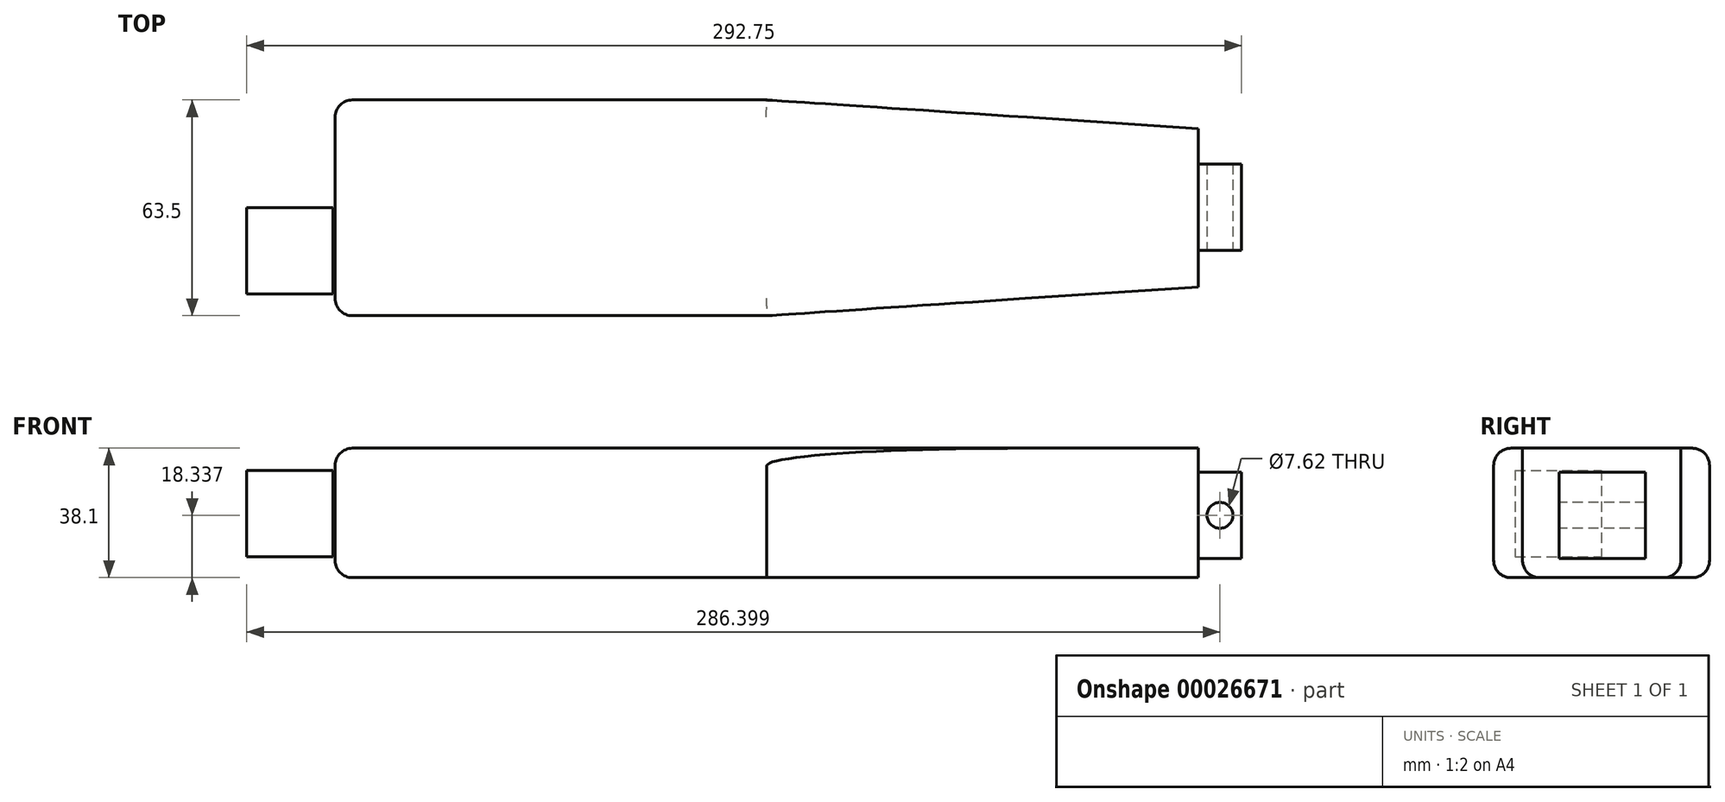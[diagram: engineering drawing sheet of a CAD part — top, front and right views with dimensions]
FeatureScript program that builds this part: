
annotation { "Feature Type Name" : "Feature", "Feature Type Description" : "" }
export const myFeature = defineFeature(function(context is Context, id is Id, definition is map)
    precondition{}
    {
        {
            var Q0;
            Q0=qCreatedBy(makeId("Front.planeOp"),FACE);
            var sketch = newSketch(context, id + "F0", { "sketchPlane" : qUnion([Q0])});
            skLineSegment(sketch, "E0.bottom", {"start": v(-21.65, 10.24) * mm, "end": v(3.75, 10.24) * mm});
            skLineSegment(sketch, "E0.top", {"start": v(-21.65, -15.16) * mm, "end": v(3.75, -15.16) * mm});
            skLineSegment(sketch, "E0.left", {"start": v(-21.65, 10.24) * mm, "end": v(-21.65, -15.16) * mm});
            skLineSegment(sketch, "E0.right", {"start": v(3.75, 10.24) * mm, "end": v(3.75, -15.16) * mm});
            skSolve(sketch);
        }
        {
            var Q0;
            Q0 = qSketchRegion(id + "F0", true);
            extrude(context, id + "F1", {"entities" : qUnion([Q0]), "depth" : 25.4 * mm});
        }
        {
            var Q0;
            Q0=qCreatedBy(makeId("Front.planeOp"),FACE);
            var sketch = newSketch(context, id + "F2", { "sketchPlane" : qUnion([Q0])});
            skLineSegment(sketch, "E1.bottom", {"start": v(4.4, 16.73) * mm, "end": v(258.4, 16.73) * mm});
            skLineSegment(sketch, "E1.top", {"start": v(4.4, -21.37) * mm, "end": v(258.4, -21.37) * mm});
            skLineSegment(sketch, "E1.left", {"start": v(4.4, 16.73) * mm, "end": v(4.4, -21.37) * mm});
            skLineSegment(sketch, "E1.right", {"start": v(258.4, 16.73) * mm, "end": v(258.4, -21.37) * mm});
            skPoint(sketch, "E2", {"position": v(4.4, -15.02) * mm});
            skPoint(sketch, "E3", {"position": v(4.4, 10.38) * mm});
            skSolve(sketch);
        }
        {
            var Q0;
            Q0 = qSketchRegion(id + "F2", true);
            extrude(context, id + "F3", {"entities" : qUnion([Q0]), "depth" : 31.75 * mm});
        }
        {
            var Q0;
            Q0 = qSketchRegion(id + "F2", true);
            extrude(context, id + "F4", {"entities" : qUnion([Q0]), "operationType" : NewBodyOperationType.ADD, "oppositeDirection" : true, "depth" : 31.75 * mm});
        }
        {
            var Q0;
            {var subQ0=sQuery(id+"F2.wireOp",EDGE,"E1.bottom");Q0=makeQuery(id+"F4.boolean.opBoolean","MERGE",FACE,{"derivedFrom":[makeQuery(id+"F3.opExtrude","SWEPT_FACE",FACE,{"disambiguationData":[OSD([subQ0])]}),makeQuery(id+"F4.opExtrude","SWEPT_FACE",FACE,{"disambiguationData":[OSD([subQ0])]})]});}
            var sketch = newSketch(context, id + "F5", { "sketchPlane" : qUnion([Q0])});
            skLineSegment(sketch, "E4", {"start": v(131.4, -31.75) * mm, "end": v(258.4, -23.26) * mm});
            skLineSegment(sketch, "E5", {"start": v(258.4, -23.26) * mm, "end": v(258.4, -31.75) * mm});
            skLineSegment(sketch, "E6", {"start": v(258.4, -31.75) * mm, "end": v(131.4, -31.75) * mm});
            skSolve(sketch);
        }
        {
            var Q0;
            Q0=makeQuery(id+"F5.imprint","IMPRINT",FACE,{"disambiguationData":[TD([[makeQuery(id+"F5.imprint","IMPRINT",EDGE,{"derivedFrom":sQuery(id+"F5.wireOp",EDGE,"E4")}),-1.0]])]});
            extrude(context, id + "F6", {"entities" : qUnion([Q0]), "operationType" : NewBodyOperationType.REMOVE, "endBound" : BoundingType.THROUGH_ALL, "oppositeDirection" : true, "depth" : 25.4 * mm});
        }
        {
            var Q0;
            {var subQ0=sQuery(id+"F2.wireOp",EDGE,"E1.bottom");Q0=makeQuery(id+"F4.boolean.opBoolean","MERGE",FACE,{"derivedFrom":[makeQuery(id+"F3.opExtrude","SWEPT_FACE",FACE,{"disambiguationData":[OSD([subQ0])]}),makeQuery(id+"F4.opExtrude","SWEPT_FACE",FACE,{"disambiguationData":[OSD([subQ0])]})]});}
            var sketch = newSketch(context, id + "F7", { "sketchPlane" : qUnion([Q0])});
            skLineSegment(sketch, "E7", {"start": v(131.4, 31.75) * mm, "end": v(258.4, 23.32) * mm});
            skLineSegment(sketch, "E8", {"start": v(258.4, 23.32) * mm, "end": v(258.4, 31.75) * mm});
            skLineSegment(sketch, "E9", {"start": v(258.4, 31.75) * mm, "end": v(131.4, 31.75) * mm});
            skSolve(sketch);
        }
        {
            var Q0;
            Q0=makeQuery(id+"F7.imprint","IMPRINT",FACE,{"disambiguationData":[TD([[makeQuery(id+"F7.imprint","IMPRINT",EDGE,{"derivedFrom":sQuery(id+"F7.wireOp",EDGE,"E7")}),1.0]])]});
            extrude(context, id + "F8", {"entities" : qUnion([Q0]), "operationType" : NewBodyOperationType.REMOVE, "endBound" : BoundingType.THROUGH_ALL, "oppositeDirection" : true, "depth" : 25.4 * mm});
        }
        {
            var Q0;
            Q0=makeQuery(id+"F3.opExtrude","CAP_EDGE",EDGE,{"disambiguationData":[OSD([sQuery(id+"F2.wireOp",EDGE,"E1.bottom")])],"isStart":false});
            var Q1;
            Q1=makeQuery(id+"F6.boolean.opBoolean","COPY",EDGE,{"derivedFrom":makeQuery(id+"F6.opExtrude","CAP_EDGE",EDGE,{"disambiguationData":[OSD([sQuery(id+"F5.wireOp",EDGE,"E4")])],"isStart":true})});
            var Q2;
            Q2=makeQuery(id+"F8.boolean.opBoolean","COPY",EDGE,{"derivedFrom":makeQuery(id+"F8.opExtrude","CAP_EDGE",EDGE,{"disambiguationData":[OSD([sQuery(id+"F7.wireOp",EDGE,"E7")])],"isStart":true})});
            var Q3;
            Q3=makeQuery(id+"F4.opExtrude","CAP_EDGE",EDGE,{"disambiguationData":[OSD([sQuery(id+"F2.wireOp",EDGE,"E1.bottom")])],"isStart":false});
            var Q4;
            {var subQ0=sQuery(id+"F2.wireOp",EDGE,"E1.bottom");var subQ1=sQuery(id+"F2.wireOp",EDGE,"E1.left");Q4=makeQuery(id+"F4.boolean.opBoolean","MERGE",EDGE,{"derivedFrom":[makeQuery(id+"F3.opExtrude","SWEPT_EDGE",EDGE,{"disambiguationData":[OSD([subQ0,subQ1])]}),makeQuery(id+"F4.opExtrude","SWEPT_EDGE",EDGE,{"disambiguationData":[OSD([subQ0,subQ1])]})]});}
            var Q5;
            Q5=makeQuery(id+"F8.boolean.opBoolean","COPY",EDGE,{"derivedFrom":makeQuery(id+"F8.opExtrude","SWEPT_EDGE",EDGE,{"disambiguationData":[OSD([sQuery(id+"F2.wireOp",EDGE,"E1.bottom"),sQuery(id+"F7.wireOp",EDGE,"E7"),sQuery(id+"F7.wireOp",EDGE,"E9")])]})});
            var Q6;
            Q6=makeQuery(id+"F3.opExtrude","CAP_EDGE",EDGE,{"disambiguationData":[OSD([sQuery(id+"F2.wireOp",EDGE,"E1.top")])],"isStart":false});
            var Q7;
            {var subQ0=sQuery(id+"F2.wireOp",EDGE,"E1.top");Q7=makeQuery(id+"F6.boolean.opBoolean","INTERSECT",EDGE,{"derivedFrom":[makeQuery(id+"F4.boolean.opBoolean","MERGE",FACE,{"derivedFrom":[makeQuery(id+"F3.opExtrude","SWEPT_FACE",FACE,{"disambiguationData":[OSD([subQ0])]}),makeQuery(id+"F4.opExtrude","SWEPT_FACE",FACE,{"disambiguationData":[OSD([subQ0])]})]}),makeQuery(id+"F6.opExtrude","SWEPT_FACE",FACE,{"disambiguationData":[OSD([sQuery(id+"F5.wireOp",EDGE,"E4")])]})]});}
            var Q8;
            Q8=makeQuery(id+"F4.opExtrude","CAP_EDGE",EDGE,{"disambiguationData":[OSD([sQuery(id+"F2.wireOp",EDGE,"E1.top")])],"isStart":false});
            var Q9;
            {var subQ0=sQuery(id+"F2.wireOp",EDGE,"E1.top");Q9=makeQuery(id+"F8.boolean.opBoolean","INTERSECT",EDGE,{"derivedFrom":[makeQuery(id+"F4.boolean.opBoolean","MERGE",FACE,{"derivedFrom":[makeQuery(id+"F3.opExtrude","SWEPT_FACE",FACE,{"disambiguationData":[OSD([subQ0])]}),makeQuery(id+"F4.opExtrude","SWEPT_FACE",FACE,{"disambiguationData":[OSD([subQ0])]})]}),makeQuery(id+"F8.opExtrude","SWEPT_FACE",FACE,{"disambiguationData":[OSD([sQuery(id+"F7.wireOp",EDGE,"E7")])]})]});}
            var Q10;
            {var subQ0=sQuery(id+"F2.wireOp",EDGE,"E1.top");var subQ1=sQuery(id+"F2.wireOp",EDGE,"E1.left");Q10=makeQuery(id+"F4.boolean.opBoolean","MERGE",EDGE,{"derivedFrom":[makeQuery(id+"F3.opExtrude","SWEPT_EDGE",EDGE,{"disambiguationData":[OSD([subQ0,subQ1])]}),makeQuery(id+"F4.opExtrude","SWEPT_EDGE",EDGE,{"disambiguationData":[OSD([subQ0,subQ1])]})]});}
            var Q11;
            Q11=makeQuery(id+"F3.opExtrude","CAP_EDGE",EDGE,{"disambiguationData":[OSD([sQuery(id+"F2.wireOp",EDGE,"E1.left")])],"isStart":false});
            var Q12;
            Q12=makeQuery(id+"F4.opExtrude","CAP_EDGE",EDGE,{"disambiguationData":[OSD([sQuery(id+"F2.wireOp",EDGE,"E1.left")])],"isStart":false});
            fillet(context, id + "F9", {"entities" : qUnion([Q0, Q1, Q2, Q3, Q4, Q5, Q6, Q7, Q8, Q9, Q10, Q11, Q12]), "radius" : 5.08 * mm, "tangentPropagation" : true, "allowEdgeOverflow" : false});
        }
        {
            var Q0;
            {var subQ0=sQuery(id+"F2.wireOp",EDGE,"E1.right");Q0=makeQuery(id+"F4.boolean.opBoolean","MERGE",FACE,{"derivedFrom":[makeQuery(id+"F3.opExtrude","SWEPT_FACE",FACE,{"disambiguationData":[OSD([subQ0])]}),makeQuery(id+"F4.opExtrude","SWEPT_FACE",FACE,{"disambiguationData":[OSD([subQ0])]})]});}
            var sketch = newSketch(context, id + "F10", { "sketchPlane" : qUnion([Q0])});
            skLineSegment(sketch, "E10.bottom", {"start": v(-12.52, 9.67) * mm, "end": v(12.88, 9.67) * mm});
            skLineSegment(sketch, "E10.top", {"start": v(-12.52, -15.73) * mm, "end": v(12.88, -15.73) * mm});
            skLineSegment(sketch, "E10.left", {"start": v(-12.52, 9.67) * mm, "end": v(-12.52, -15.73) * mm});
            skLineSegment(sketch, "E10.right", {"start": v(12.88, 9.67) * mm, "end": v(12.88, -15.73) * mm});
            skPoint(sketch, "E11", {"position": v(0.18, -15.73) * mm});
            skSolve(sketch);
        }
        {
            var Q0;
            Q0 = qSketchRegion(id + "F10", true);
            extrude(context, id + "F11", {"entities" : qUnion([Q0]), "operationType" : NewBodyOperationType.ADD, "depth" : 12.7 * mm});
        }
        {
            var Q0;
            Q0=makeQuery(id+"F11.opExtrude","SWEPT_FACE",FACE,{"disambiguationData":[OSD([sQuery(id+"F10.wireOp",EDGE,"E10.left")])]});
            var sketch = newSketch(context, id + "F12", { "sketchPlane" : qUnion([Q0])});
            skCircle(sketch, "E12", {"center": v(264.75, -3.03) * mm, "radius": 3.81 * mm});
            skSolve(sketch);
        }
        {
            var Q0;
            Q0=makeQuery(id+"F12.imprint","IMPRINT",FACE,{"disambiguationData":[TD([[makeQuery(id+"F12.imprint","IMPRINT",EDGE,{"derivedFrom":sQuery(id+"F12.wireOp",EDGE,"E12")}),1.0]])]});
            extrude(context, id + "F13", {"entities" : qUnion([Q0]), "operationType" : NewBodyOperationType.REMOVE, "endBound" : BoundingType.THROUGH_ALL, "oppositeDirection" : true, "depth" : 25.4 * mm});
        }
    });
